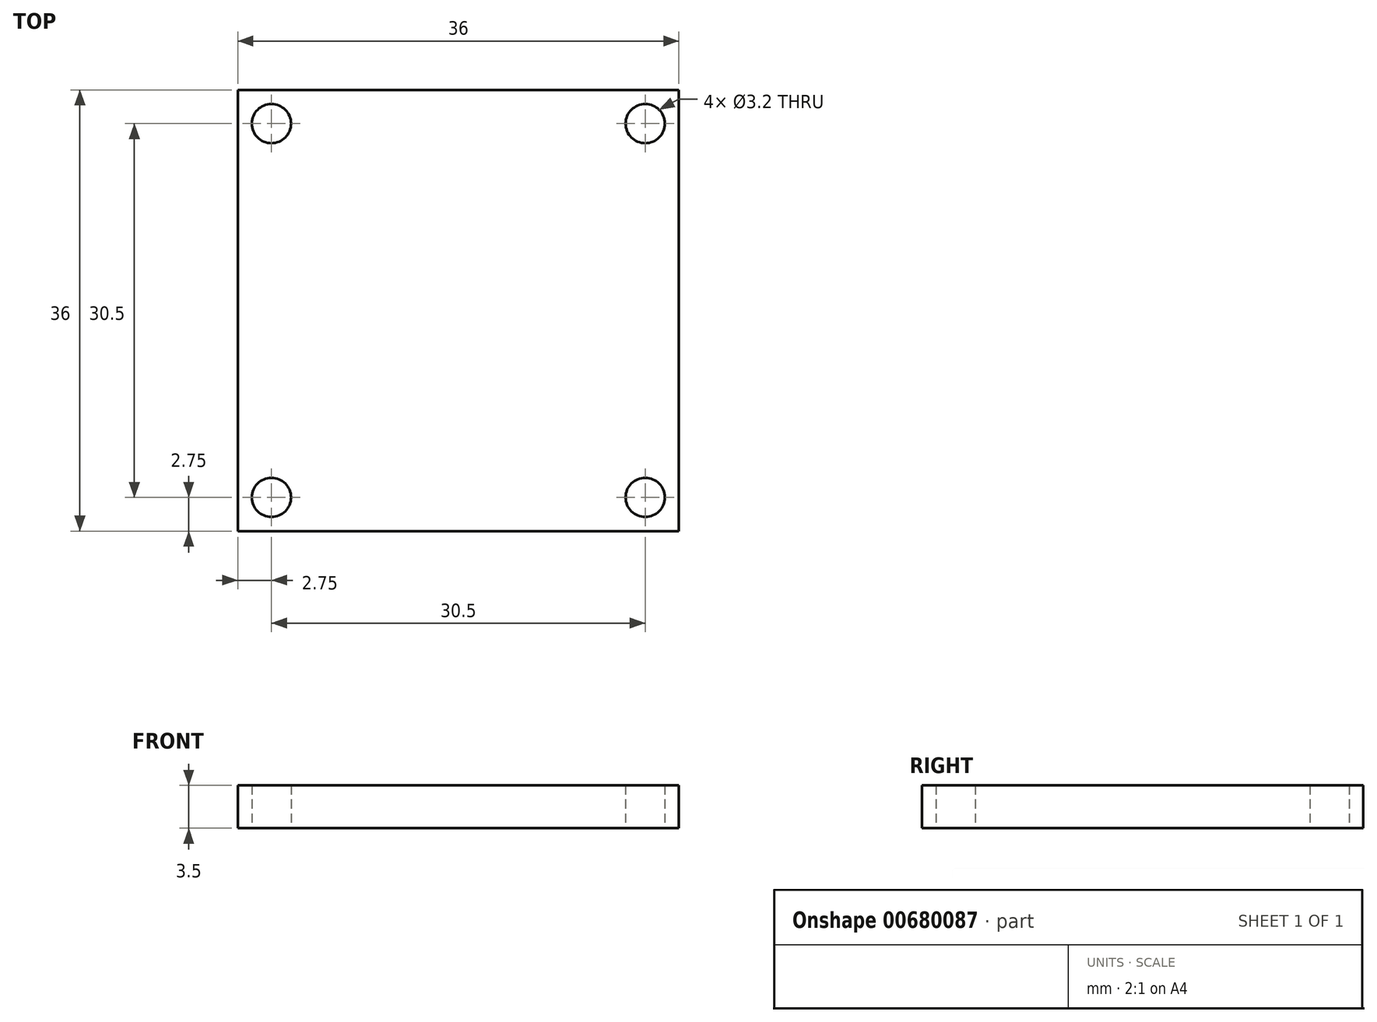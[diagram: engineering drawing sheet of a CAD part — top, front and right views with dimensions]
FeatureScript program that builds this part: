
annotation { "Feature Type Name" : "Feature", "Feature Type Description" : "" }
export const myFeature = defineFeature(function(context is Context, id is Id, definition is map)
    precondition{}
    {
        {
            var Q0;
            Q0=qCreatedBy(makeId("Top.planeOp"),FACE);
            var sketch = newSketch(context, id + "F0", { "sketchPlane" : qUnion([Q0])});
            skLineSegment(sketch, "E0.bottom", {"start": v(18, -18) * mm, "end": v(-18, -18) * mm});
            skLineSegment(sketch, "E0.top", {"start": v(18, 18) * mm, "end": v(-18, 18) * mm});
            skLineSegment(sketch, "E0.left", {"start": v(18, -18) * mm, "end": v(18, 18) * mm});
            skLineSegment(sketch, "E0.right", {"start": v(-18, -18) * mm, "end": v(-18, 18) * mm});
            skPoint(sketch, "E0.middle", {"position": v(0, 0) * mm});
            skCircle(sketch, "E1", {"center": v(15.25, 15.25) * mm, "radius": 1.6 * mm});
            skCircle(sketch, "E2.MirrorC", {"center": v(15.25, -15.25) * mm, "radius": 1.6 * mm});
            skCircle(sketch, "E3.MirrorC", {"center": v(-15.25, 15.25) * mm, "radius": 1.6 * mm});
            skCircle(sketch, "E4.MirrorC", {"center": v(-15.25, -15.25) * mm, "radius": 1.6 * mm});
            skSolve(sketch);
        }
        {
            var Q0;
            Q0=makeQuery(id+"F0.imprint","IMPRINT",FACE,{"disambiguationData":[TD([[makeQuery(id+"F0.imprint","IMPRINT",EDGE,{"derivedFrom":sQuery(id+"F0.wireOp",EDGE,"E0.bottom")}),-1.0]])]});
            extrude(context, id + "F1", {"entities" : qUnion([Q0]), "depth" : 3.5 * mm, "offsetDistance" : 25.4 * mm});
        }
    });
